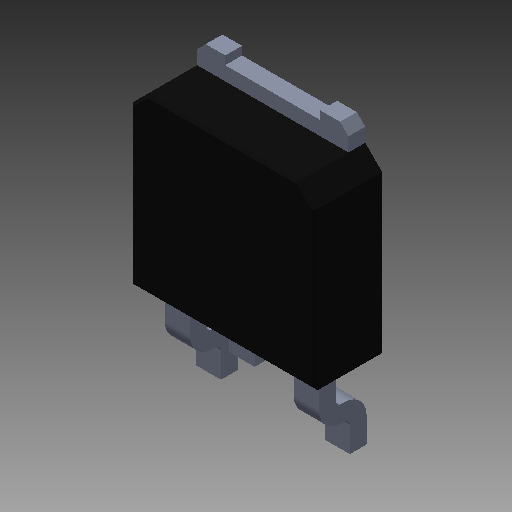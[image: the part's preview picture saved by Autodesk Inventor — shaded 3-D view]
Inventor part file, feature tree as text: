
AUTODESK INVENTOR PART (.ipt)
format: ipt  version: 2018 (Build 220112000, 112)  size: 215,552 bytes
history: native  units: mm
features: chamfer x1, imported_body x1
ambient origin geometry x8: Origin, YZ Plane, XZ Plane, XY Plane, X Axis, Y Axis, Z Axis, Center Point
bodies: Body1 (feature_tree)
feature tree (2):
  chamfer  "Fase4"  [1 undecoded]
  imported_body  "Base1"
note: 1 required parameter value undecoded (feature->parameter linkage not recoverable at this tier; creation-order binding heuristic only, values carry confidence <= 0.55)
